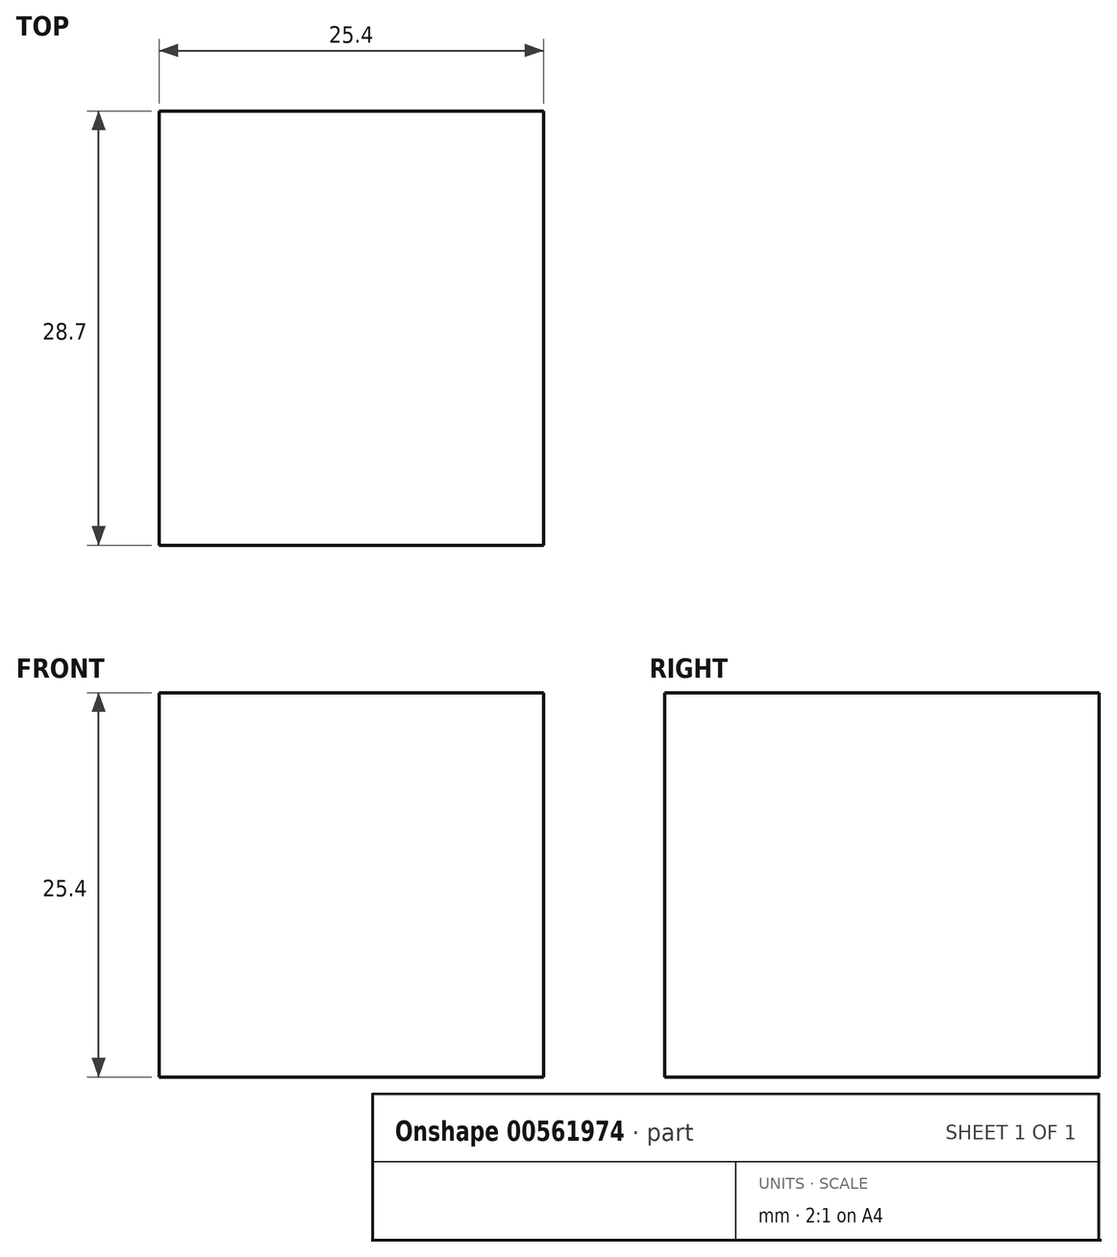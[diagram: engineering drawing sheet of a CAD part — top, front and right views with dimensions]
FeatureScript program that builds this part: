
annotation { "Feature Type Name" : "Feature", "Feature Type Description" : "" }
export const myFeature = defineFeature(function(context is Context, id is Id, definition is map)
    precondition{}
    {
        {
            var Q0;
            Q0=qCreatedBy(makeId("Front.planeOp"),FACE);
            var sketch = newSketch(context, id + "F0", { "sketchPlane" : qUnion([Q0])});
            skLineSegment(sketch, "E0.bottom", {"start": v(-27.87, 25.4) * mm, "end": v(-2.47, 25.4) * mm});
            skLineSegment(sketch, "E0.top", {"start": v(-27.87, 0) * mm, "end": v(-2.47, 0) * mm});
            skLineSegment(sketch, "E0.left", {"start": v(-27.87, 25.4) * mm, "end": v(-27.87, 0) * mm});
            skLineSegment(sketch, "E0.right", {"start": v(-2.47, 25.4) * mm, "end": v(-2.47, 0) * mm});
            skSolve(sketch);
        }
        {
            var Q0;
            Q0=makeQuery(id+"F0.imprint","IMPRINT",FACE,{"disambiguationData":[TD([[makeQuery(id+"F0.imprint","IMPRINT",EDGE,{"derivedFrom":sQuery(id+"F0.wireOp",EDGE,"E0.bottom")}),-1.0]])]});
            extrude(context, id + "F1", {"entities" : qUnion([Q0]), "oppositeDirection" : true, "depth" : 28.7 * mm, "offsetDistance" : 25.4 * mm});
        }
    });
